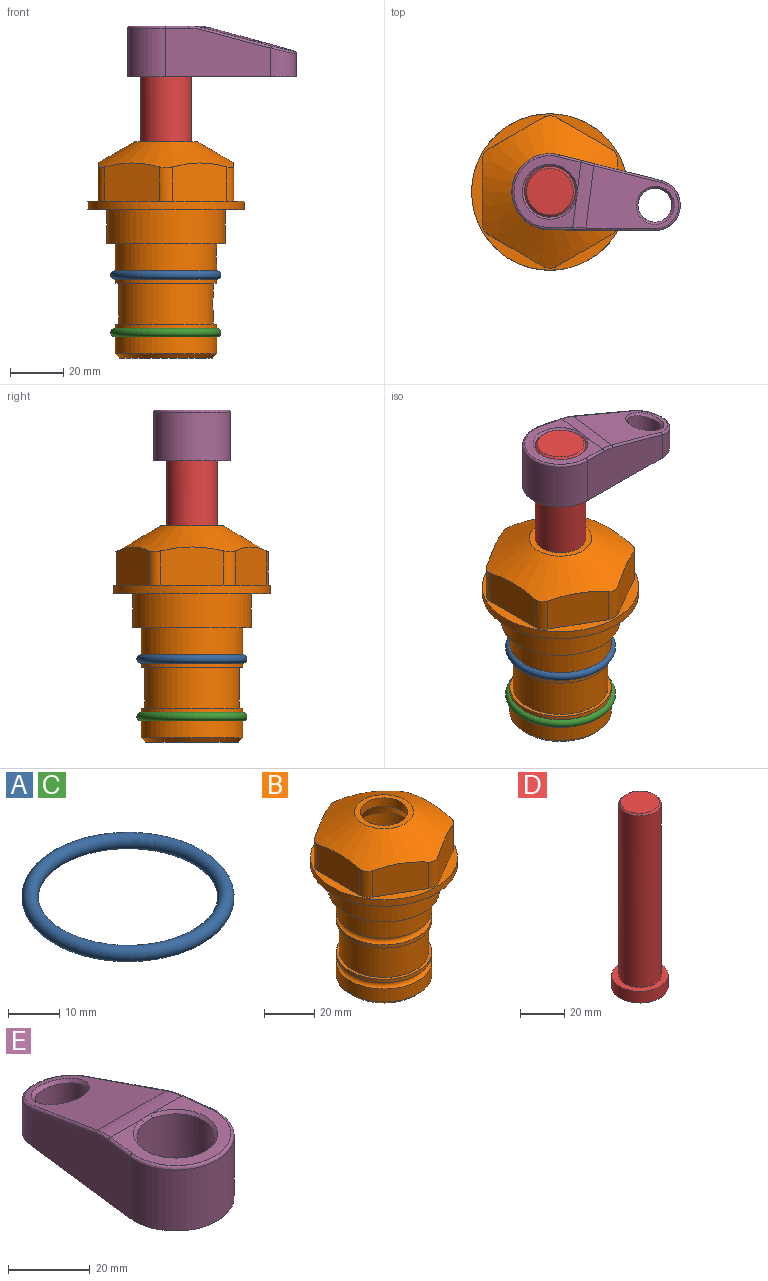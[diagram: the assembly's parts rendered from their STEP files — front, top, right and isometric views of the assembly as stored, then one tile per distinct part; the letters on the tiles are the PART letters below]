
ASSEMBLY  parts=5 mates=4
PART A: 1 faces, bbox 44.7x44.7x3.2 mm
  f0: torus R=19.05mm, axis (0,0,1), area 1193.9mm2
PART B: 36 faces, bbox 58.7x58.7x81 mm
  f0: cylinder r=17.78mm len=35.56mm, axis (0,0,1), area 1670.8mm2, adj f23,f24,f31
  f1: cylinder r=19.05mm len=38.1mm, axis (0,0,1), area 1191.9mm2, adj f26,f27,f30
  f2: plane 58.66x58.66mm, normal (0,0,-1), area 1150.6mm2, adj f3,f28
  f3: cylinder r=29.33mm len=58.66mm, axis (0,0,-1), area 585.1mm2, adj f2,f4
  f4: plane 58.66x58.66mm, normal (0,0,1), area 475.9mm2, adj f3,f5,f6,f7,f8,f9,f10,f11
  f5: plane 20.32x14.34mm, normal (-0.5,0.87,0), area 324.4mm2, adj f4,f15,f16,f17
  f6: plane 20.32x14.34mm, normal (0.5,0.87,0), area 324.4mm2, adj f4,f14,f15,f17
  f7: plane 23.48x14.34mm, normal (1,0,0), area 324.4mm2, adj f4,f13,f14,f17
  f8: plane 20.32x14.34mm, normal (0.5,-0.87,0), area 324.4mm2, adj f4,f12,f13,f17
  f9: plane 20.32x14.34mm, normal (-0.5,-0.87,0), area 324.4mm2, adj f4,f11,f12,f17
  f10: plane 23.48x14.34mm, normal (-1,0,0), area 324.4mm2, adj f4,f11,f16,f17
  f11: cylinder r=5.08mm len=12.85mm, axis (0,0,-1), area 67.2mm2, adj f4,f9,f10,f17
  f12: cylinder r=5.08mm len=12.85mm, axis (0,0,-1), area 67.2mm2, adj f4,f8,f9,f17
  f13: cylinder r=5.08mm len=12.85mm, axis (0,0,-1), area 67.2mm2, adj f4,f7,f8,f17
  f14: cylinder r=5.08mm len=12.85mm, axis (0,0,-1), area 67.2mm2, adj f4,f6,f7,f17
  f15: cylinder r=5.08mm len=12.85mm, axis (0,0,-1), area 67.2mm2, adj f4,f5,f6,f17
  f16: cylinder r=5.08mm len=12.85mm, axis (0,0,-1), area 67.2mm2, adj f4,f5,f10,f17
  f17: cone r=11.73mm half-angle=60deg, axis (0,0,-1), area 2071.8mm2, adj f5,f6,f7,f8,f9,f10,f11,f12
  f18: plane 23.46x23.46mm, normal (0,0,1), area 147.4mm2, adj f17,f35
  f19: plane 34.93x34.93mm, normal (0,0,-1), area 958mm2, adj f29
  f20: cylinder r=19.05mm len=38.1mm, axis (0,0,1), area 760.1mm2, adj f21,f29
  f21: torus R=19.05mm, axis (0,0,1), area 565.3mm2, adj f20,f22
  f22: cylinder r=19.05mm len=38.1mm, axis (0,0,1), area 190mm2, adj f21,f23
  f23: plane 38.1x38.1mm, normal (0,0,1), area 146.9mm2, adj f0,f22
  f24: plane 38.1x38.1mm, normal (0,0,-1), area 146.9mm2, adj f0,f25
  f25: cylinder r=19.05mm len=38.1mm, axis (0,0,1), area 190mm2, adj f24,f26
  f26: torus R=19.05mm, axis (0,0,1), area 565.3mm2, adj f1,f25
  f27: plane 44.45x44.45mm, normal (0,0,-1), area 411.7mm2, adj f1,f28
  f28: cylinder r=22.23mm len=44.45mm, axis (0,0,1), area 1773.5mm2, adj f2,f27
  f29: cone r=19.05mm half-angle=45deg, axis (0,0,1), area 257.5mm2, adj f19,f20
  f30: cylinder r=3.17mm len=6.75mm, axis (-1,0,0), area 128mm2, adj f1,f33
  f31: cylinder r=3.17mm len=6.35mm, axis (-1,0,0), area 102.5mm2, adj f0,f33
  f32: plane 25.4x25.4mm, normal (0,0,1), area 506.7mm2, adj f33
  f33: cylinder r=12.7mm len=66.42mm, axis (0,0,-1), area 5236.2mm2, adj f30,f31,f32,f34
  f34: cone r=9.53mm half-angle=30deg, axis (0,0,-1), area 443.4mm2, adj f33,f35
  f35: cylinder r=9.53mm len=19.05mm, axis (0,0,-1), area 240.9mm2, adj f18,f34
PART C: same geometry as A
PART D: 6 faces, bbox 25.4x25.4x101.6 mm
  f0: plane 17.46x17.46mm, normal (0,0,1), area 239.5mm2, adj f5
  f1: plane 25.4x25.4mm, normal (0,0,-1), area 506.7mm2, adj f2
  f2: cylinder r=12.7mm len=25.4mm, axis (0,0,1), area 506.7mm2, adj f1,f3
  f3: plane 25.4x25.4mm, normal (0,0,1), area 221.7mm2, adj f2,f4
  f4: cylinder r=9.53mm len=94.46mm, axis (0,0,1), area 5653mm2, adj f3,f5
  f5: cone r=8.73mm half-angle=45deg, axis (0,0,-1), area 64.4mm2, adj f0,f4
PART E: 31 faces, bbox 31.7x65.5x19.8 mm
  f0: plane 39.12x18.26mm, normal (0.99,0.12,0), area 612.2mm2, adj f1,f4,f7,f11,f13,f15
  f1: cylinder r=9.53mm len=18.91mm, axis (0,0,-1), area 296.1mm2, adj f0,f2,f7,f17
  f2: plane 39.12x18.26mm, normal (-0.99,0.12,0), area 612.2mm2, adj f1,f4,f7,f12,f14,f16
  f3: cylinder r=6.35mm len=12.7mm, axis (0,0,-1), area 362.4mm2, adj f7,f18
  f4: cylinder r=14.29mm len=28.58mm, axis (0,0,-1), area 882.2mm2, adj f0,f2,f7,f10
  f5: cylinder r=9.53mm len=19.05mm, axis (0,0,-1), area 1092.6mm2, adj f7,f19,f20
  f6: plane 26.99x23.69mm, normal (0,0,1), area 216.2mm2, adj f9,f10,f11,f12,f19
  f7: plane 63.5x28.58mm, normal (0,0,-1), area 661.8mm2, adj f0,f1,f2,f3,f4,f5,f22,f23
  f8: plane 33.52x23.6mm, normal (0,0.26,0.97), area 486mm2, adj f9,f15,f16,f17,f18
  f9: cylinder r=19.05mm len=24.72mm, axis (1,0,0), area 120.4mm2, adj f6,f8,f13,f14,f20
  f10: torus R=13.49mm, axis (0,0,1), area 59mm2, adj f4,f6,f11,f12
  f11: cylinder r=0.79mm len=8.67mm, axis (0.12,-0.99,0), area 10.8mm2, adj f0,f6,f10,f13
  f12: cylinder r=0.79mm len=8.67mm, axis (0.12,0.99,0), area 10.8mm2, adj f2,f6,f10,f14
  f13: bspline ~4.95x1.42mm, area 6.1mm2, adj f0,f9,f11,f15
  f14: bspline ~4.95x1.42mm, area 6.1mm2, adj f2,f9,f12,f16
  f15: cylinder r=0.79mm len=25.95mm, axis (0.12,-0.96,0.26), area 32.9mm2, adj f0,f8,f13,f17
  f16: cylinder r=0.79mm len=25.95mm, axis (0.12,0.96,-0.26), area 32.9mm2, adj f2,f8,f14,f17
  f17: bspline ~18.91x8.38mm, area 30mm2, adj f1,f8,f15,f16
  f18: bspline ~14.29x14.29mm, area 48.3mm2, adj f3,f8
  f19: cone r=9.53mm half-angle=45deg, axis (0,0,1), area 66.5mm2, adj f5,f6,f20
  f20: bspline ~3.22x0.96mm, area 3.5mm2, adj f5,f9,f19
  f21: plane 2.75x2.72mm, normal (0,0,-1), area 2.9mm2, adj f23,f25,f28
  f22: plane 23.05x15.88mm, normal (-0.99,-0.12,0), area 323.6mm2, adj f7,f25,f26,f27,f28,f29
  f23: plane 23.05x15.88mm, normal (0.99,-0.12,0), area 323.6mm2, adj f7,f21,f25,f27,f28,f30
  f24: cylinder r=9.53mm len=10.69mm, axis (0,0,-1), area 114.7mm2, adj f7,f27,f29,f30
  f25: cylinder r=12.7mm len=20.59mm, axis (0,0,-1), area 381.1mm2, adj f7,f21,f22,f23,f26,f28
  f26: plane 2.75x2.72mm, normal (0,0,-1), area 2.9mm2, adj f22,f25,f28
  f27: plane 19.72x18.37mm, normal (0,-0.26,-0.97), area 291.8mm2, adj f22,f23,f24,f28,f29,f30
  f28: cylinder r=15.88mm len=19.92mm, axis (1,0,0), area 54.8mm2, adj f21,f22,f23,f25,f26,f27
  f29: cylinder r=1.59mm len=11mm, axis (0,0,-1), area 34.7mm2, adj f7,f22,f24,f27
  f30: cylinder r=1.59mm len=11mm, axis (0,0,-1), area 34.7mm2, adj f7,f23,f24,f27
PLACE A rot(axis=(0,0,1),90deg) t=(0,0,0)mm
PLACE B at identity fixed
PLACE C rot(axis=(0,0,1),90deg) t=(0,0,-21.59)mm
PLACE D rot(axis=(0,0,-1),97.3deg) t=(0,0,5.34)mm
PLACE E rot(axis=(0,0,-1),97.3deg) t=(0,0,5.34)mm
MATE fastened C.f0 <-> B.f0  axis (0,0,1) through (0,0,-46.1)mm
MATE cylindrical B.f0 <-> D.f2  axis (0,0,1) through (0,0,-50.55)mm
MATE fastened A.f0 <-> B.f0  axis (0,0,1) through (0,0,-24.51)mm
MATE fastened E.f4 <-> D.f2  axis (0,0,1) through (0,0,68.84)mm
